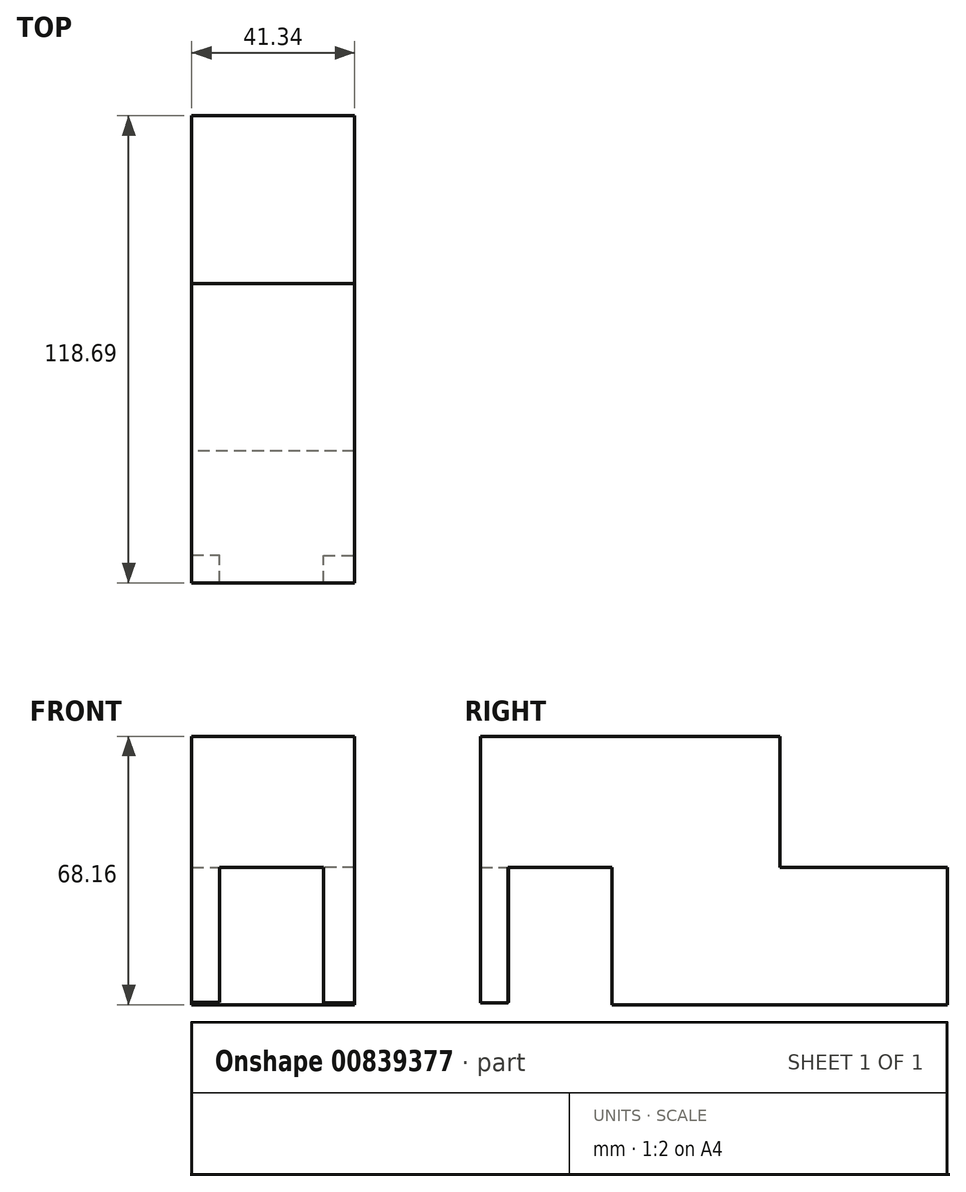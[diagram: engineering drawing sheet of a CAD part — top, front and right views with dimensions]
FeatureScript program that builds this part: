
annotation { "Feature Type Name" : "Feature", "Feature Type Description" : "" }
export const myFeature = defineFeature(function(context is Context, id is Id, definition is map)
    precondition{}
    {
        {
            var Q0;
            Q0=qCreatedBy(makeId("Top.planeOp"),FACE);
            var sketch = newSketch(context, id + "F0", { "sketchPlane" : qUnion([Q0])});
            skLineSegment(sketch, "E0.bottom", {"start": v(41.34, 42.96) * mm, "end": v(0, 42.96) * mm});
            skLineSegment(sketch, "E0.top", {"start": v(41.34, -42.27) * mm, "end": v(0, -42.27) * mm});
            skLineSegment(sketch, "E0.left", {"start": v(41.34, 42.96) * mm, "end": v(41.34, -42.27) * mm});
            skLineSegment(sketch, "E0.right", {"start": v(0, 42.96) * mm, "end": v(0, -42.27) * mm});
            skSolve(sketch);
        }
        {
            var Q0;
            Q0 = qSketchRegion(id + "F0", true);
            extrude(context, id + "F1", {"entities" : qUnion([Q0]), "depth" : 34.9 * mm, "offsetDistance" : 25.4 * mm});
        }
        {
            var Q0;
            Q0=makeQuery(id+"F1.opExtrude","CAP_FACE",FACE,{"disambiguationData":[OSD([sQuery(id+"F0.wireOp",EDGE,"E0.bottom"),sQuery(id+"F0.wireOp",EDGE,"E0.top"),sQuery(id+"F0.wireOp",EDGE,"E0.left"),sQuery(id+"F0.wireOp",EDGE,"E0.right")])],"isStart":false});
            var sketch = newSketch(context, id + "F2", { "sketchPlane" : qUnion([Q0])});
            skLineSegment(sketch, "E1.bottom", {"start": v(41.34, 0.35) * mm, "end": v(0, 0.35) * mm});
            skLineSegment(sketch, "E1.top", {"start": v(41.34, -75.73) * mm, "end": v(0, -75.73) * mm});
            skLineSegment(sketch, "E1.left", {"start": v(41.34, 0.35) * mm, "end": v(41.34, -75.73) * mm});
            skLineSegment(sketch, "E1.right", {"start": v(0, 0.35) * mm, "end": v(0, -75.73) * mm});
            skSolve(sketch);
        }
        {
            var Q0;
            Q0 = qSketchRegion(id + "F2", true);
            extrude(context, id + "F3", {"entities" : qUnion([Q0]), "operationType" : NewBodyOperationType.ADD, "depth" : 33.27 * mm, "offsetDistance" : 25.4 * mm});
        }
        {
            var Q0;
            Q0=makeQuery(id+"F3.opExtrude","CAP_FACE",FACE,{"disambiguationData":[OSD([sQuery(id+"F2.wireOp",EDGE,"E1.bottom"),sQuery(id+"F2.wireOp",EDGE,"E1.top"),sQuery(id+"F2.wireOp",EDGE,"E1.left"),sQuery(id+"F2.wireOp",EDGE,"E1.right")])],"isStart":true});
            var sketch = newSketch(context, id + "F4", { "sketchPlane" : qUnion([Q0])});
            skLineSegment(sketch, "E2.bottom", {"start": v(0, 75.73) * mm, "end": v(7.09, 75.73) * mm});
            skLineSegment(sketch, "E2.top", {"start": v(0, 68.58) * mm, "end": v(7.09, 68.58) * mm});
            skLineSegment(sketch, "E2.left", {"start": v(0, 75.73) * mm, "end": v(0, 68.58) * mm});
            skLineSegment(sketch, "E2.right", {"start": v(7.09, 75.73) * mm, "end": v(7.09, 68.58) * mm});
            skSolve(sketch);
        }
        {
            var Q0;
            Q0 = qSketchRegion(id + "F4", true);
            extrude(context, id + "F5", {"entities" : qUnion([Q0]), "operationType" : NewBodyOperationType.ADD, "depth" : 34.33 * mm, "offsetDistance" : 25.4 * mm});
        }
        {
            var Q0;
            Q0=makeQuery(id+"F3.opExtrude","CAP_FACE",FACE,{"disambiguationData":[OSD([sQuery(id+"F2.wireOp",EDGE,"E1.bottom"),sQuery(id+"F2.wireOp",EDGE,"E1.top"),sQuery(id+"F2.wireOp",EDGE,"E1.left"),sQuery(id+"F2.wireOp",EDGE,"E1.right")])],"isStart":true});
            var sketch = newSketch(context, id + "F6", { "sketchPlane" : qUnion([Q0])});
            skLineSegment(sketch, "E3.bottom", {"start": v(33.45, 75.73) * mm, "end": v(41.34, 75.73) * mm});
            skLineSegment(sketch, "E3.top", {"start": v(33.45, 68.79) * mm, "end": v(41.34, 68.79) * mm});
            skLineSegment(sketch, "E3.left", {"start": v(33.45, 75.73) * mm, "end": v(33.45, 68.79) * mm});
            skLineSegment(sketch, "E3.right", {"start": v(41.34, 75.73) * mm, "end": v(41.34, 68.79) * mm});
            skSolve(sketch);
        }
        {
            var Q0;
            Q0=makeQuery(id+"F6.imprint","IMPRINT",FACE,{"disambiguationData":[TD([[makeQuery(id+"F6.imprint","IMPRINT",EDGE,{"derivedFrom":sQuery(id+"F6.wireOp",EDGE,"E3.bottom")}),1.0]])]});
            extrude(context, id + "F7", {"entities" : qUnion([Q0]), "operationType" : NewBodyOperationType.ADD, "depth" : 34.4 * mm, "offsetDistance" : 25.4 * mm});
        }
    });
